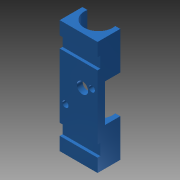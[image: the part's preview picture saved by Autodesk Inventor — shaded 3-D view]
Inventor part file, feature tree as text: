
AUTODESK INVENTOR PART (.ipt)
format: ipt  version: 2013 SP2 (Build 170200200, 200)  size: 134,656 bytes
history: native  units: mm
features: extrude x4, sketch x4, reference x1
ambient origin geometry x8: Origin, YZ Plane, XZ Plane, XY Plane, X Axis, Y Axis, Z Axis, Center Point
bodies: Solid1 (feature_tree)
feature tree (9):
  extrude  "Extrusion1"  Depth=12.0mm
  extrude  "Extrusion4"  Depth=60.0mm TaperAngle=0.0deg
  extrude  "Extrusion5"  Depth=20.0mm
  extrude  "Extrusion6"  Depth=3.2mm
  sketch  "Sketch1"  dims[d0=20.0mm d1=12.0mm]
  sketch  "Sketch4"  dims[d2=15.0mm d4=60.0mm d5=0.0mm]
  sketch  "Sketch5"  dims[d14=1.5mm d15=20.0mm]
  sketch  "Sketch6"  dims[d17=8.0mm d18=0.0mm d19=3.2mm d20=3.2mm d21=3.0mm d22=3.0mm d23=10.0mm d24=0.0mm d25=6.0mm d26=1.5mm d27=6.0mm d28=10.0mm d29=0.0mm d30=6.0mm]
  reference  "Reference1"
